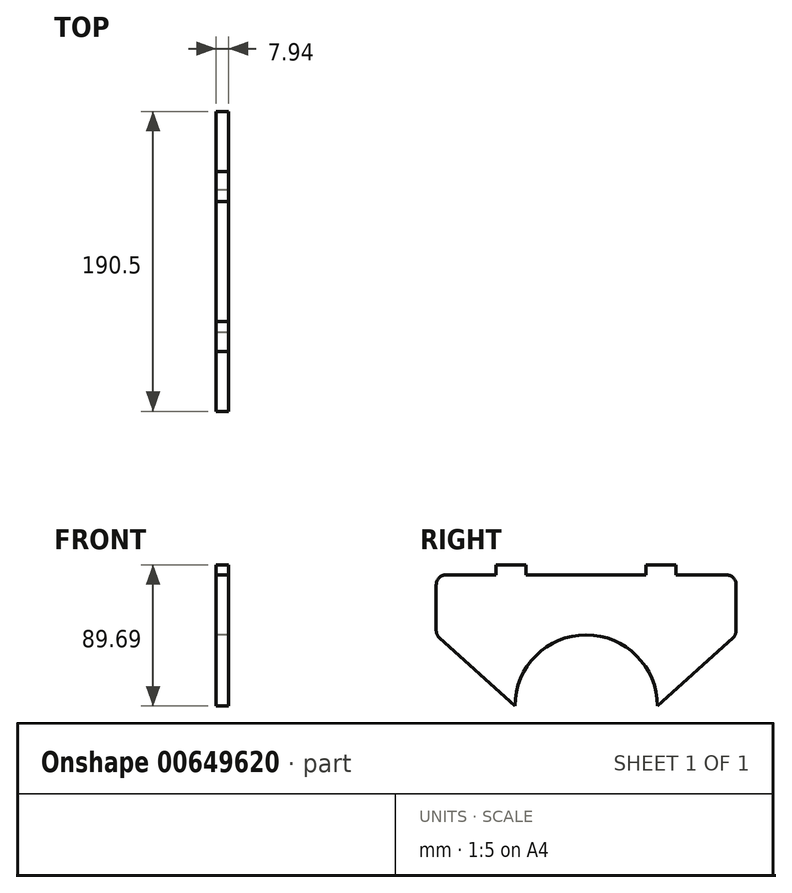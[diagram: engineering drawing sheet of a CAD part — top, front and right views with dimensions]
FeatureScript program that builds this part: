
annotation { "Feature Type Name" : "Feature", "Feature Type Description" : "" }
export const myFeature = defineFeature(function(context is Context, id is Id, definition is map)
    precondition{}
    {
        {
            var Q0;
            Q0=qCreatedBy(makeId("Right.planeOp"),FACE);
            var sketch = newSketch(context, id + "F0", { "sketchPlane" : qUnion([Q0])});
            skArc(sketch, "E0", {"start": v(45.24, 0) * mm, "mid": v(0, 45.24) * mm, "end": v(-45.24, 0) * mm});
            skLineSegment(sketch, "E1", {"start": v(-88.9, 83.34) * mm, "end": v(-57.15, 83.34) * mm});
            skLineSegment(sketch, "E2", {"start": v(0, 45.24) * mm, "end": v(0, 83.34) * mm, "construction": true});
            skLineSegment(sketch, "E3", {"start": v(57.15, 83.34) * mm, "end": v(57.15, 89.7) * mm});
            skLineSegment(sketch, "E4", {"start": v(57.15, 89.7) * mm, "end": v(38.1, 89.7) * mm});
            skLineSegment(sketch, "E5", {"start": v(38.1, 89.7) * mm, "end": v(38.1, 83.34) * mm});
            skLineSegment(sketch, "E6", {"start": v(-38.1, 83.34) * mm, "end": v(-38.1, 89.7) * mm});
            skLineSegment(sketch, "E7", {"start": v(-38.1, 89.7) * mm, "end": v(-57.15, 89.7) * mm});
            skLineSegment(sketch, "E8", {"start": v(-57.15, 89.7) * mm, "end": v(-57.15, 83.34) * mm});
            skLineSegment(sketch, "E9", {"start": v(-95.25, 77) * mm, "end": v(-95.25, 48.06) * mm});
            skLineSegment(sketch, "E10", {"start": v(-93.16, 43.35) * mm, "end": v(-45.24, 0) * mm});
            skLineSegment(sketch, "E11", {"start": v(95.25, 77) * mm, "end": v(95.25, 48.06) * mm});
            skLineSegment(sketch, "E12", {"start": v(93.16, 43.35) * mm, "end": v(45.24, 0) * mm});
            skLineSegment(sketch, "E13.trimOffspring", {"start": v(-38.1, 83.34) * mm, "end": v(38.1, 83.34) * mm});
            skLineSegment(sketch, "E14.trimOffspring", {"start": v(57.15, 83.34) * mm, "end": v(88.9, 83.34) * mm});
            skPoint(sketch, "E15.visualSharp", {"position": v(-95.25, 83.34) * mm});
            skArc(sketch, "E15.filletArc", {"start": v(-88.9, 83.34) * mm, "mid": v(-93.4, 81.48) * mm, "end": v(-95.25, 77) * mm});
            skPoint(sketch, "E16.visualSharp", {"position": v(-95.25, 45.24) * mm});
            skArc(sketch, "E16.filletArc", {"start": v(-95.25, 48.06) * mm, "mid": v(-94.7, 45.49) * mm, "end": v(-93.16, 43.35) * mm});
            skPoint(sketch, "E17.visualSharp", {"position": v(95.25, 45.24) * mm});
            skArc(sketch, "E17.filletArc", {"start": v(93.16, 43.35) * mm, "mid": v(94.7, 45.49) * mm, "end": v(95.25, 48.06) * mm});
            skPoint(sketch, "E18.visualSharp", {"position": v(95.25, 83.34) * mm});
            skArc(sketch, "E18.filletArc", {"start": v(95.25, 77) * mm, "mid": v(93.4, 81.48) * mm, "end": v(88.9, 83.34) * mm});
            skLineSegment(sketch, "E19", {"start": v(-57.15, 83.34) * mm, "end": v(57.15, 83.34) * mm, "construction": true});
            skSolve(sketch);
        }
        {
            var Q0;
            Q0=qSketchRegion(id+"F0",true);
            extrude(context, id + "F1", {"entities" : qUnion([Q0]), "depth" : 7.94 * mm, "offsetDistance" : 25.4 * mm});
        }
    });
